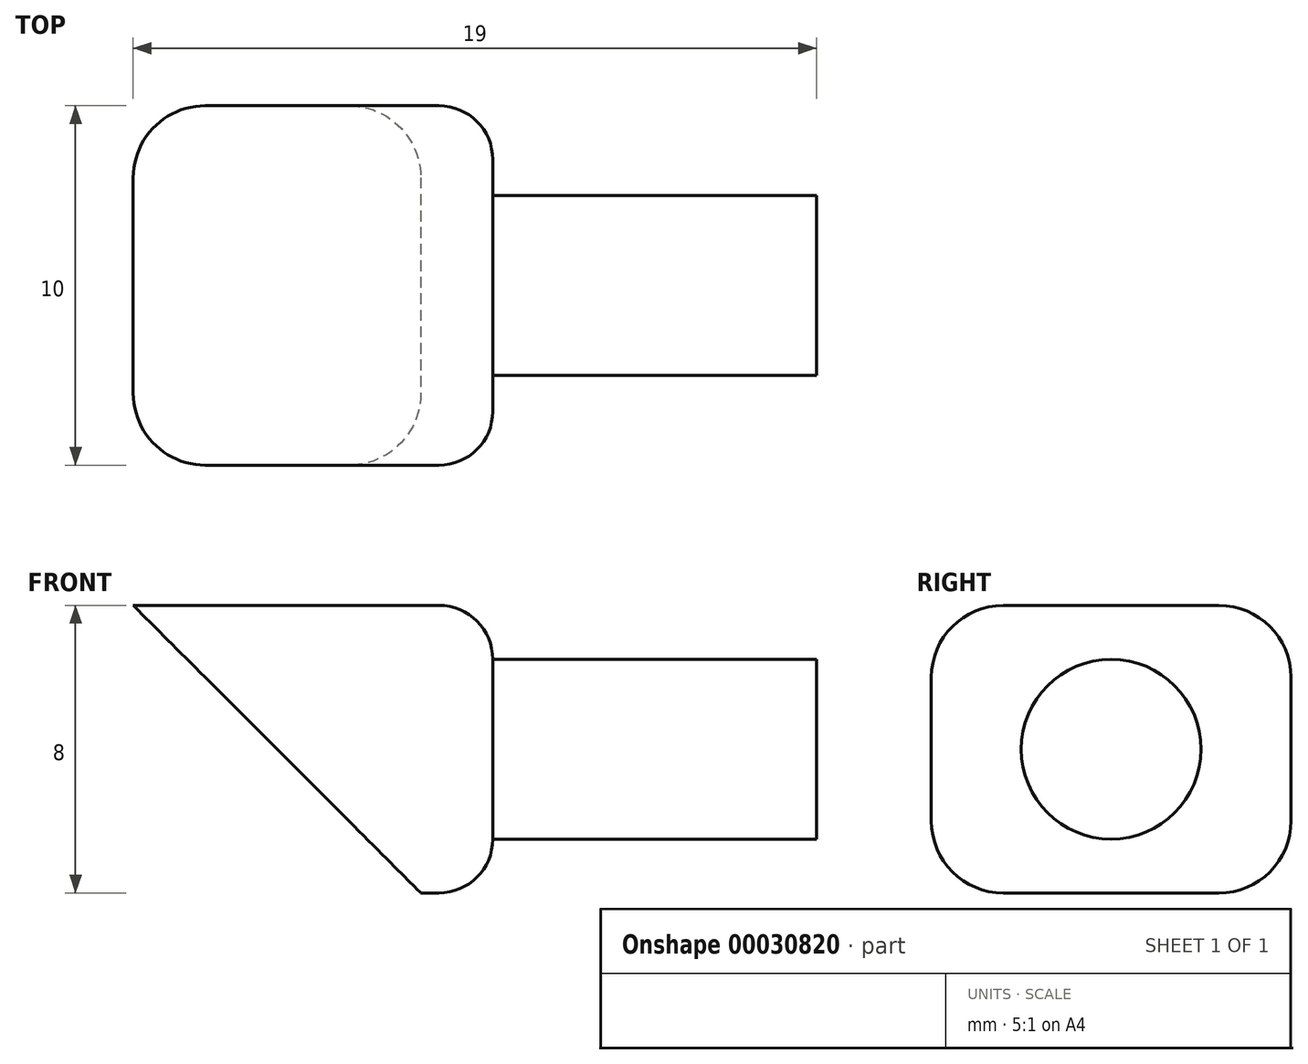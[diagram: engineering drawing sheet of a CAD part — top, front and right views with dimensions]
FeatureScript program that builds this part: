
annotation { "Feature Type Name" : "Feature", "Feature Type Description" : "" }
export const myFeature = defineFeature(function(context is Context, id is Id, definition is map)
    precondition{}
    {
        {
            var Q0;
            Q0=qCreatedBy(makeId("Front.planeOp"),FACE);
            var sketch = newSketch(context, id + "F0", { "sketchPlane" : qUnion([Q0])});
            skLineSegment(sketch, "E0.bottom", {"start": v(-5, 4) * mm, "end": v(5, 4) * mm});
            skLineSegment(sketch, "E0.top", {"start": v(-5, -4) * mm, "end": v(5, -4) * mm});
            skLineSegment(sketch, "E0.left", {"start": v(-5, 4) * mm, "end": v(-5, -4) * mm});
            skLineSegment(sketch, "E0.right", {"start": v(5, 4) * mm, "end": v(5, -4) * mm});
            skLineSegment(sketch, "E1", {"start": v(-5, 4) * mm, "end": v(5, -4) * mm, "construction": true});
            skSolve(sketch);
        }
        {
            var Q0;
            Q0 = qSketchRegion(id + "F0", true);
            extrude(context, id + "F1", {"entities" : qUnion([Q0]), "endBound" : BoundingType.SYMMETRIC, "depth" : 10 * mm});
        }
        {
            var Q0;
            Q0=makeQuery(id+"F1.opExtrude","CAP_FACE",FACE,{"disambiguationData":[OSD([sQuery(id+"F0.wireOp",EDGE,"E0.bottom"),sQuery(id+"F0.wireOp",EDGE,"E0.top"),sQuery(id+"F0.wireOp",EDGE,"E0.left"),sQuery(id+"F0.wireOp",EDGE,"E0.right")])],"isStart":false});
            var sketch = newSketch(context, id + "F2", { "sketchPlane" : qUnion([Q0])});
            skLineSegment(sketch, "E2", {"start": v(-5, 4) * mm, "end": v(3, -4) * mm});
            skLineSegment(sketch, "E3", {"start": v(-5, 4) * mm, "end": v(-5, -4) * mm});
            skLineSegment(sketch, "E4", {"start": v(-5, -4) * mm, "end": v(3, -4) * mm});
            skSolve(sketch);
        }
        {
            var Q0;
            Q0 = qSketchRegion(id + "F2", true);
            extrude(context, id + "F3", {"entities" : qUnion([Q0]), "operationType" : NewBodyOperationType.REMOVE, "endBound" : BoundingType.THROUGH_ALL, "oppositeDirection" : true, "depth" : 25 * mm});
        }
        {
            var Q0;
            Q0=makeQuery(id+"F1.opExtrude","SWEPT_FACE",FACE,{"disambiguationData":[OSD([sQuery(id+"F0.wireOp",EDGE,"E0.right")])]});
            var sketch = newSketch(context, id + "F4", { "sketchPlane" : qUnion([Q0])});
            skCircle(sketch, "E5", {"center": v(0, 0) * mm, "radius": 2.5 * mm});
            skLineSegment(sketch, "E6", {"start": v(5, 4) * mm, "end": v(-5, -4) * mm, "construction": true});
            skSolve(sketch);
        }
        {
            var Q0;
            Q0 = qSketchRegion(id + "F4", true);
            extrude(context, id + "F5", {"entities" : qUnion([Q0]), "operationType" : NewBodyOperationType.ADD, "depth" : 9 * mm});
        }
        {
            var Q0;
            Q0=makeQuery(id+"F1.opExtrude","CAP_EDGE",EDGE,{"disambiguationData":[OSD([sQuery(id+"F0.wireOp",EDGE,"E0.bottom")])],"isStart":false});
            var Q1;
            Q1=makeQuery(id+"F1.opExtrude","CAP_EDGE",EDGE,{"disambiguationData":[OSD([sQuery(id+"F0.wireOp",EDGE,"E0.bottom")])],"isStart":true});
            var Q2;
            Q2=makeQuery(id+"F1.opExtrude","CAP_EDGE",EDGE,{"disambiguationData":[OSD([sQuery(id+"F0.wireOp",EDGE,"E0.top")])],"isStart":false});
            var Q3;
            Q3=makeQuery(id+"F1.opExtrude","CAP_EDGE",EDGE,{"disambiguationData":[OSD([sQuery(id+"F0.wireOp",EDGE,"E0.top")])],"isStart":true});
            fillet(context, id + "F6", {"entities" : qUnion([Q0, Q1, Q2, Q3]), "radius" : 2 * mm, "tangentPropagation" : true, "allowEdgeOverflow" : false});
        }
        {
            var Q0;
            Q0=makeQuery(id+"F1.opExtrude","CAP_EDGE",EDGE,{"disambiguationData":[OSD([sQuery(id+"F0.wireOp",EDGE,"E0.right")])],"isStart":false});
            fillet(context, id + "F7", {"entities" : qUnion([Q0]), "radius" : 1.5 * mm, "tangentPropagation" : true, "allowEdgeOverflow" : false});
        }
    });
